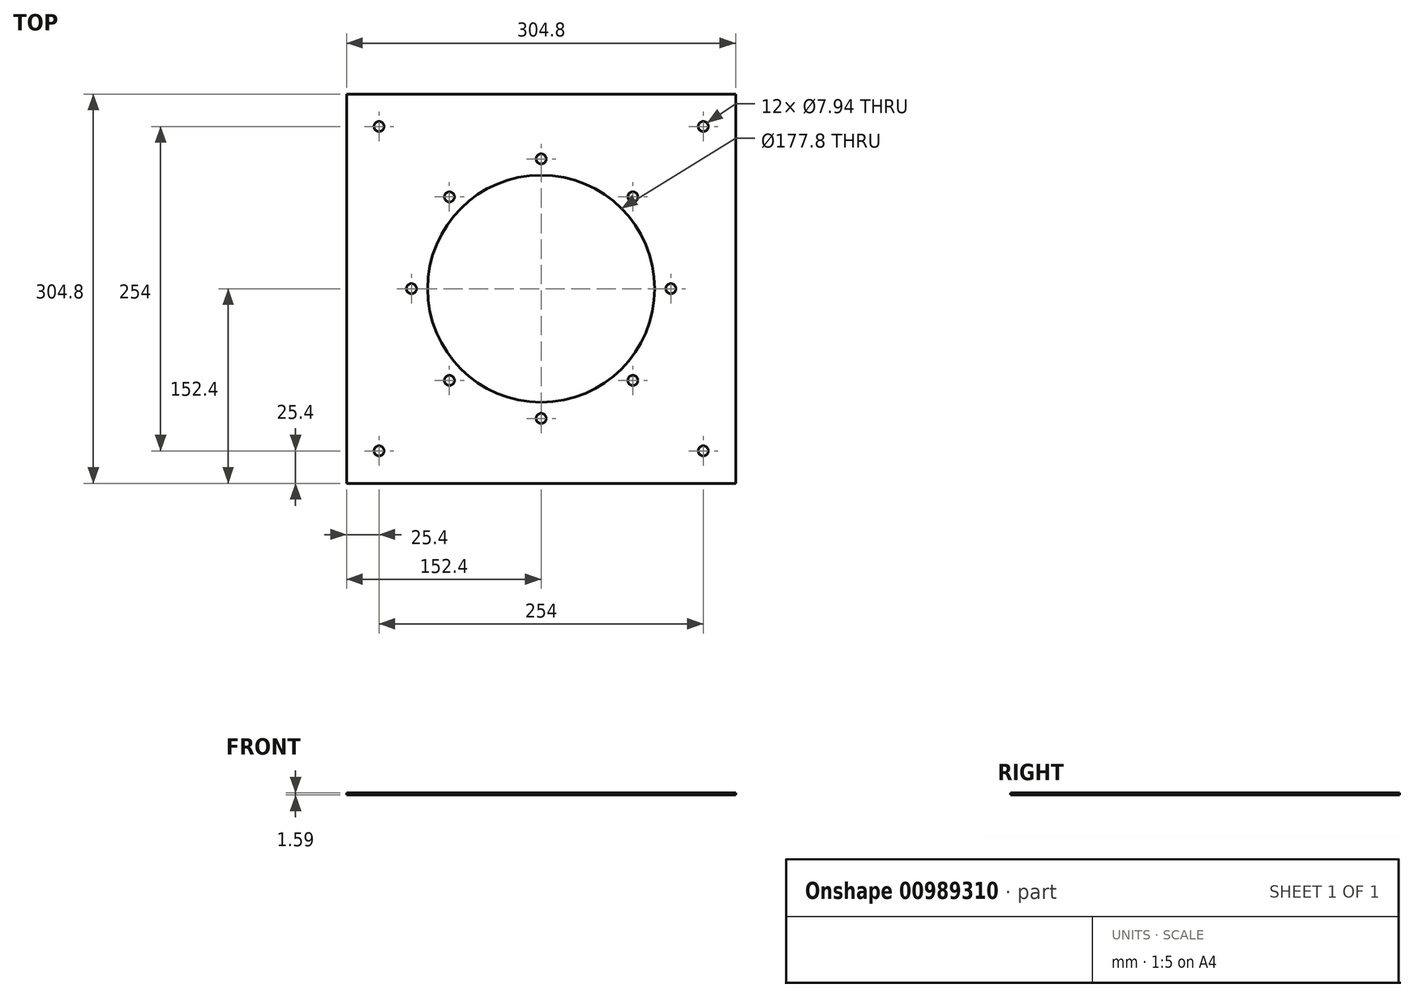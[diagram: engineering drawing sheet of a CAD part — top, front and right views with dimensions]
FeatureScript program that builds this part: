
annotation { "Feature Type Name" : "Feature", "Feature Type Description" : "" }
export const myFeature = defineFeature(function(context is Context, id is Id, definition is map)
    precondition{}
    {
        {
            var Q0;
            Q0=qCreatedBy(makeId("Top.planeOp"),FACE);
            var sketch = newSketch(context, id + "F0", { "sketchPlane" : qUnion([Q0])});
            skLineSegment(sketch, "E0.bottom", {"start": v(0, 0) * mm, "end": v(304.8, 0) * mm});
            skLineSegment(sketch, "E0.top", {"start": v(0, 304.8) * mm, "end": v(304.8, 304.8) * mm});
            skLineSegment(sketch, "E0.left", {"start": v(0, 0) * mm, "end": v(0, 304.8) * mm});
            skLineSegment(sketch, "E0.right", {"start": v(304.8, 0) * mm, "end": v(304.8, 304.8) * mm});
            skCircle(sketch, "E1", {"center": v(25.4, 279.4) * mm, "radius": 3.97 * mm});
            skCircle(sketch, "E2", {"center": v(279.4, 279.4) * mm, "radius": 3.97 * mm});
            skCircle(sketch, "E3", {"center": v(25.4, 25.4) * mm, "radius": 3.97 * mm});
            skCircle(sketch, "E4", {"center": v(279.4, 25.4) * mm, "radius": 3.97 * mm});
            skSolve(sketch);
        }
        {
            var Q0;
            Q0 = qSketchRegion(id + "F0", true);
            extrude(context, id + "F1", {"entities" : qUnion([Q0]), "depth" : 1.59 * mm, "offsetDistance" : 25.4 * mm});
        }
        {
            var Q0;
            Q0=makeQuery(id+"F1.opExtrude","CAP_FACE",FACE,{"disambiguationData":[OSD([sQuery(id+"F0.wireOp",EDGE,"E0.bottom"),sQuery(id+"F0.wireOp",EDGE,"E0.top"),sQuery(id+"F0.wireOp",EDGE,"E0.left"),sQuery(id+"F0.wireOp",EDGE,"E0.right"),sQuery(id+"F0.wireOp",EDGE,"E1"),sQuery(id+"F0.wireOp",EDGE,"E2"),sQuery(id+"F0.wireOp",EDGE,"E3"),sQuery(id+"F0.wireOp",EDGE,"E4")])],"isStart":false});
            var sketch = newSketch(context, id + "F2", { "sketchPlane" : qUnion([Q0])});
            skCircle(sketch, "E5", {"center": v(152.4, 152.4) * mm, "radius": 88.9 * mm});
            skSolve(sketch);
        }
        {
            var Q0;
            Q0 = qSketchRegion(id + "F2", true);
            extrude(context, id + "F3", {"entities" : qUnion([Q0]), "operationType" : NewBodyOperationType.REMOVE, "oppositeDirection" : true, "depth" : 25.4 * mm, "offsetDistance" : 25.4 * mm});
        }
        {
            var Q0;
            Q0=makeQuery(id+"F1.opExtrude","CAP_FACE",FACE,{"disambiguationData":[OSD([sQuery(id+"F0.wireOp",EDGE,"E0.bottom"),sQuery(id+"F0.wireOp",EDGE,"E0.top"),sQuery(id+"F0.wireOp",EDGE,"E0.left"),sQuery(id+"F0.wireOp",EDGE,"E0.right"),sQuery(id+"F0.wireOp",EDGE,"E1"),sQuery(id+"F0.wireOp",EDGE,"E2"),sQuery(id+"F0.wireOp",EDGE,"E3"),sQuery(id+"F0.wireOp",EDGE,"E4")])],"isStart":false});
            var sketch = newSketch(context, id + "F4", { "sketchPlane" : qUnion([Q0])});
            skCircle(sketch, "E6", {"center": v(152.4, 254) * mm, "radius": 3.97 * mm});
            skCircle(sketch, "E7", {"center": v(152.4, 50.8) * mm, "radius": 3.97 * mm});
            skCircle(sketch, "E8", {"center": v(50.8, 152.4) * mm, "radius": 3.97 * mm});
            skCircle(sketch, "E9", {"center": v(254, 152.4) * mm, "radius": 3.97 * mm});
            skCircle(sketch, "E10", {"center": v(80.56, 224.24) * mm, "radius": 3.97 * mm});
            skCircle(sketch, "E11", {"center": v(224.24, 80.56) * mm, "radius": 3.97 * mm});
            skCircle(sketch, "E12", {"center": v(224.24, 224.24) * mm, "radius": 3.97 * mm});
            skCircle(sketch, "E13", {"center": v(80.56, 80.56) * mm, "radius": 3.97 * mm});
            skSolve(sketch);
        }
        {
            var Q0;
            Q0 = qSketchRegion(id + "F4", true);
            extrude(context, id + "F5", {"entities" : qUnion([Q0]), "operationType" : NewBodyOperationType.REMOVE, "oppositeDirection" : true, "depth" : 25.4 * mm, "offsetDistance" : 25.4 * mm});
        }
        {
            var Q0;
            Q0 = qSketchRegion(id + "F4", true);
            extrude(context, id + "F6", {"entities" : qUnion([Q0]), "operationType" : NewBodyOperationType.REMOVE, "oppositeDirection" : true, "depth" : 25.4 * mm, "offsetDistance" : 25.4 * mm});
        }
    });
